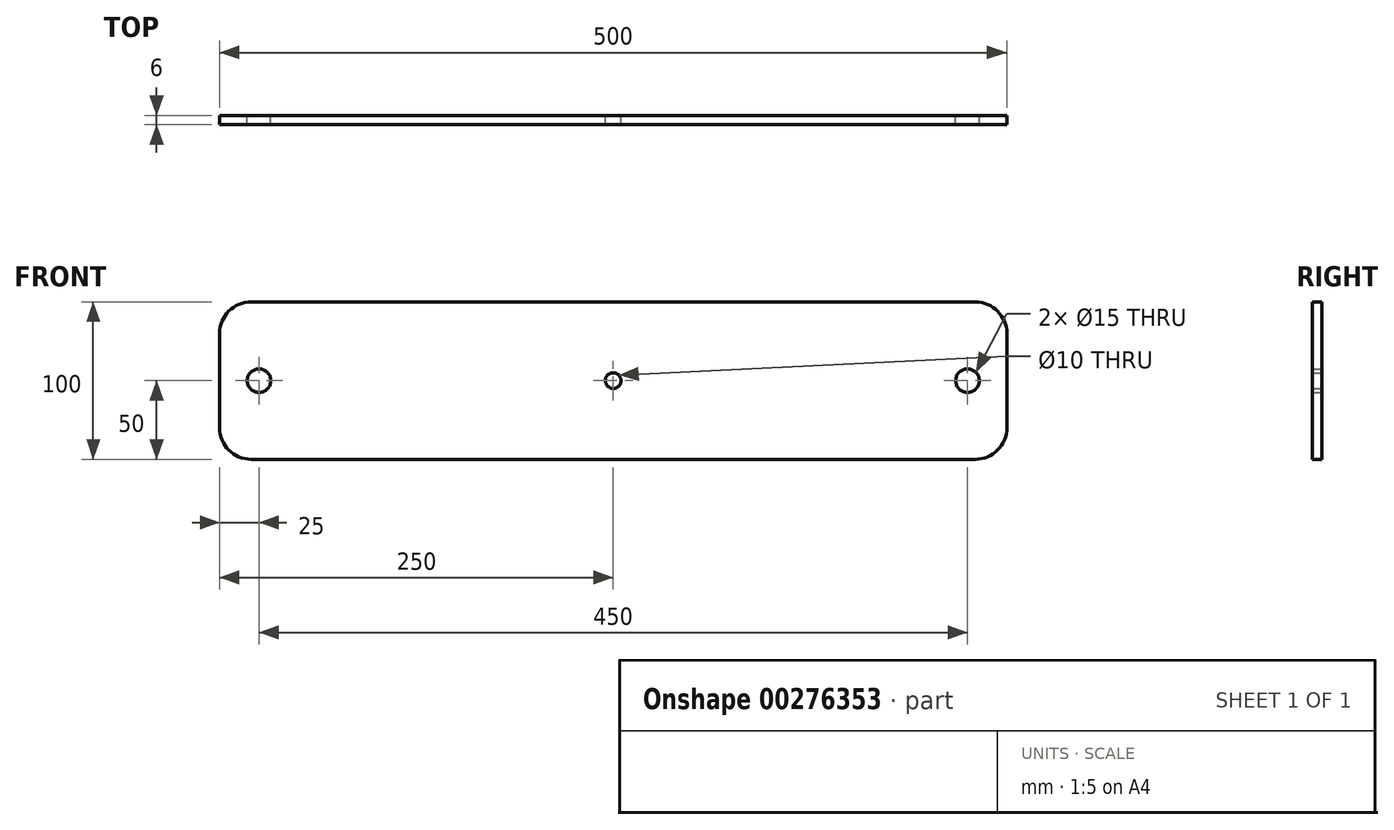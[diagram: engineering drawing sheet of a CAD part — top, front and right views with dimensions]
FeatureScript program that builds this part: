
annotation { "Feature Type Name" : "Feature", "Feature Type Description" : "" }
export const myFeature = defineFeature(function(context is Context, id is Id, definition is map)
    precondition{}
    {
        {
            var Q0;
            Q0=qCreatedBy(makeId("Front.planeOp"),FACE);
            var sketch = newSketch(context, id + "F0", { "sketchPlane" : qUnion([Q0])});
            skLineSegment(sketch, "E0.left", {"start": v(-250, 30) * mm, "end": v(-250, -30) * mm});
            skPoint(sketch, "E1.visualSharp", {"position": v(-250, 50) * mm});
            skArc(sketch, "E1.filletArc", {"start": v(-230, 50) * mm, "mid": v(-244.14, 44.14) * mm, "end": v(-250, 30) * mm});
            skPoint(sketch, "E2.visualSharp", {"position": v(-250, -50) * mm});
            skArc(sketch, "E2.filletArc", {"start": v(-250, -30) * mm, "mid": v(-244.14, -44.14) * mm, "end": v(-230, -50) * mm});
            skCircle(sketch, "E3", {"center": v(-225, 0) * mm, "radius": 7.5 * mm});
            skCircle(sketch, "E4", {"center": v(0, 0) * mm, "radius": 5 * mm});
            skCircle(sketch, "E5.MirrorC", {"center": v(225, 0) * mm, "radius": 7.5 * mm});
            skArc(sketch, "E6.MirrorCS", {"start": v(230, 50) * mm, "mid": v(244.14, 44.14) * mm, "end": v(250, 30) * mm});
            skPoint(sketch, "E7.MirrorP", {"position": v(250, 50) * mm});
            skArc(sketch, "E8.MirrorCS", {"start": v(250, -30) * mm, "mid": v(244.14, -44.14) * mm, "end": v(230, -50) * mm});
            skLineSegment(sketch, "E9", {"start": v(-230, 50) * mm, "end": v(230, 50) * mm});
            skLineSegment(sketch, "E10", {"start": v(-230, -50) * mm, "end": v(230, -50) * mm});
            skLineSegment(sketch, "E11", {"start": v(250, -30) * mm, "end": v(250, 30) * mm});
            skSolve(sketch);
        }
        {
            var Q0;
            Q0=makeQuery(id+"F0.imprint","IMPRINT",FACE,{"disambiguationData":[TD([[makeQuery(id+"F0.imprint","IMPRINT",EDGE,{"derivedFrom":sQuery(id+"F0.wireOp",EDGE,"E0.left")}),1.0]])]});
            extrude(context, id + "F1", {"entities" : qUnion([Q0]), "depth" : 6 * mm});
        }
    });
